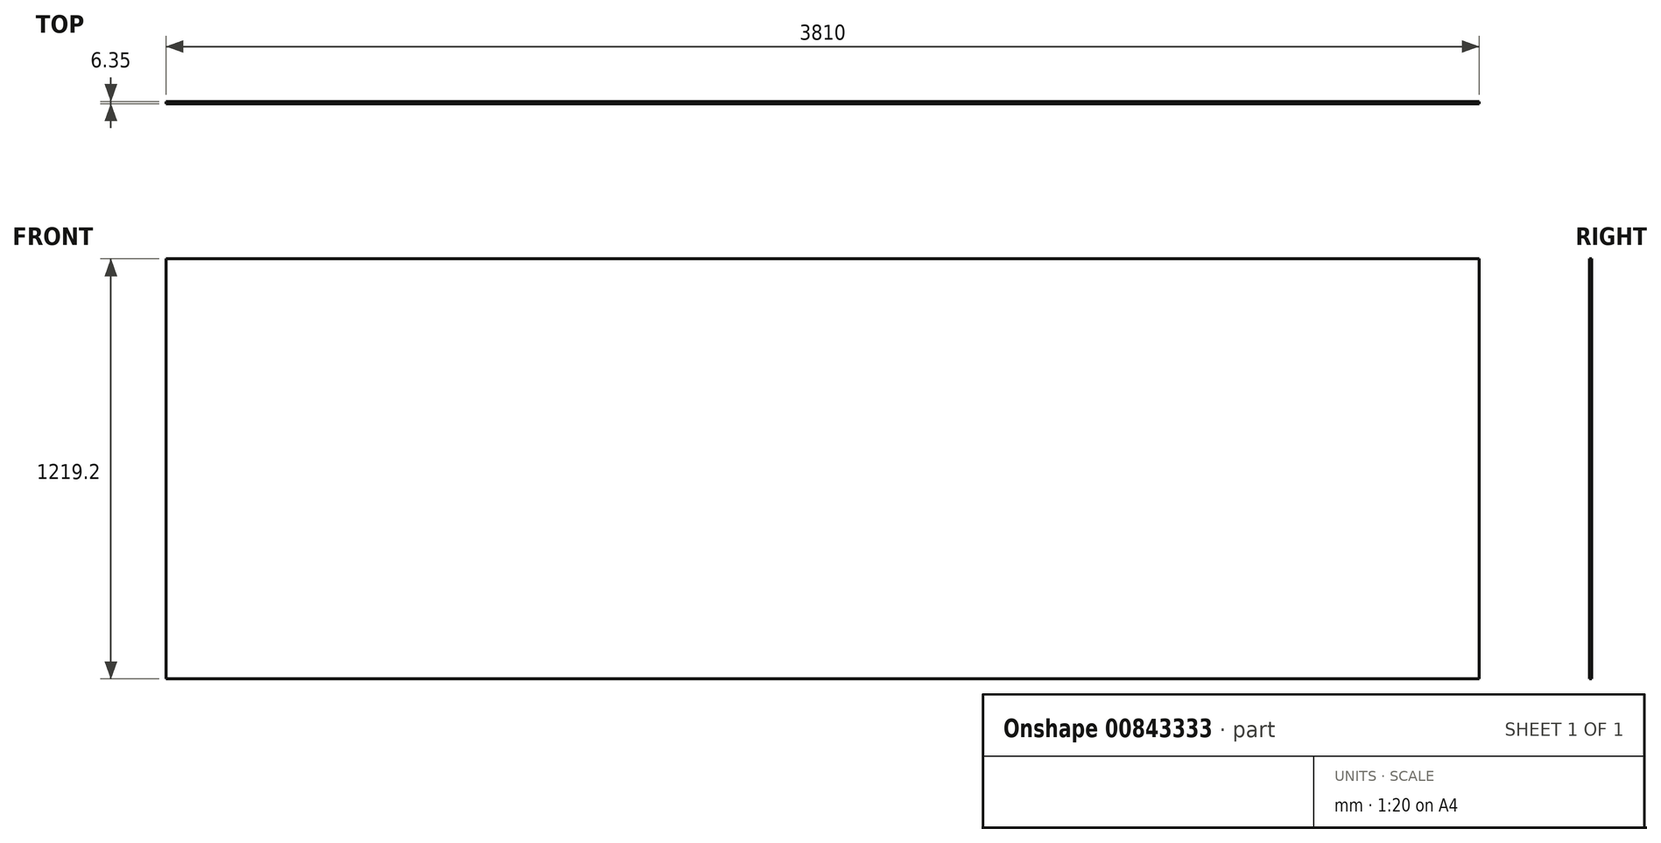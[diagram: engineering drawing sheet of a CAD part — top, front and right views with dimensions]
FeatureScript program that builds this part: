
annotation { "Feature Type Name" : "Feature", "Feature Type Description" : "" }
export const myFeature = defineFeature(function(context is Context, id is Id, definition is map)
    precondition{}
    {
        {
            var Q0;
            Q0=qCreatedBy(makeId("Front.planeOp"),FACE);
            var sketch = newSketch(context, id + "F0", { "sketchPlane" : qUnion([Q0])});
            skLineSegment(sketch, "E0.bottom", {"start": v(1905, -612.7) * mm, "end": v(-1905, -612.7) * mm});
            skLineSegment(sketch, "E0.top", {"start": v(1905, 606.5) * mm, "end": v(-1905, 606.5) * mm});
            skLineSegment(sketch, "E0.left", {"start": v(1905, -612.7) * mm, "end": v(1905, 606.5) * mm});
            skLineSegment(sketch, "E0.right", {"start": v(-1905, -612.7) * mm, "end": v(-1905, 606.5) * mm});
            skPoint(sketch, "E0.middle", {"position": v(0, -3.1) * mm});
            skSolve(sketch);
        }
        {
            var Q0;
            Q0 = qSketchRegion(id + "F0", true);
            extrude(context, id + "F1", {"entities" : qUnion([Q0]), "depth" : 6.35 * mm, "offsetDistance" : 25.4 * mm});
        }
    });
